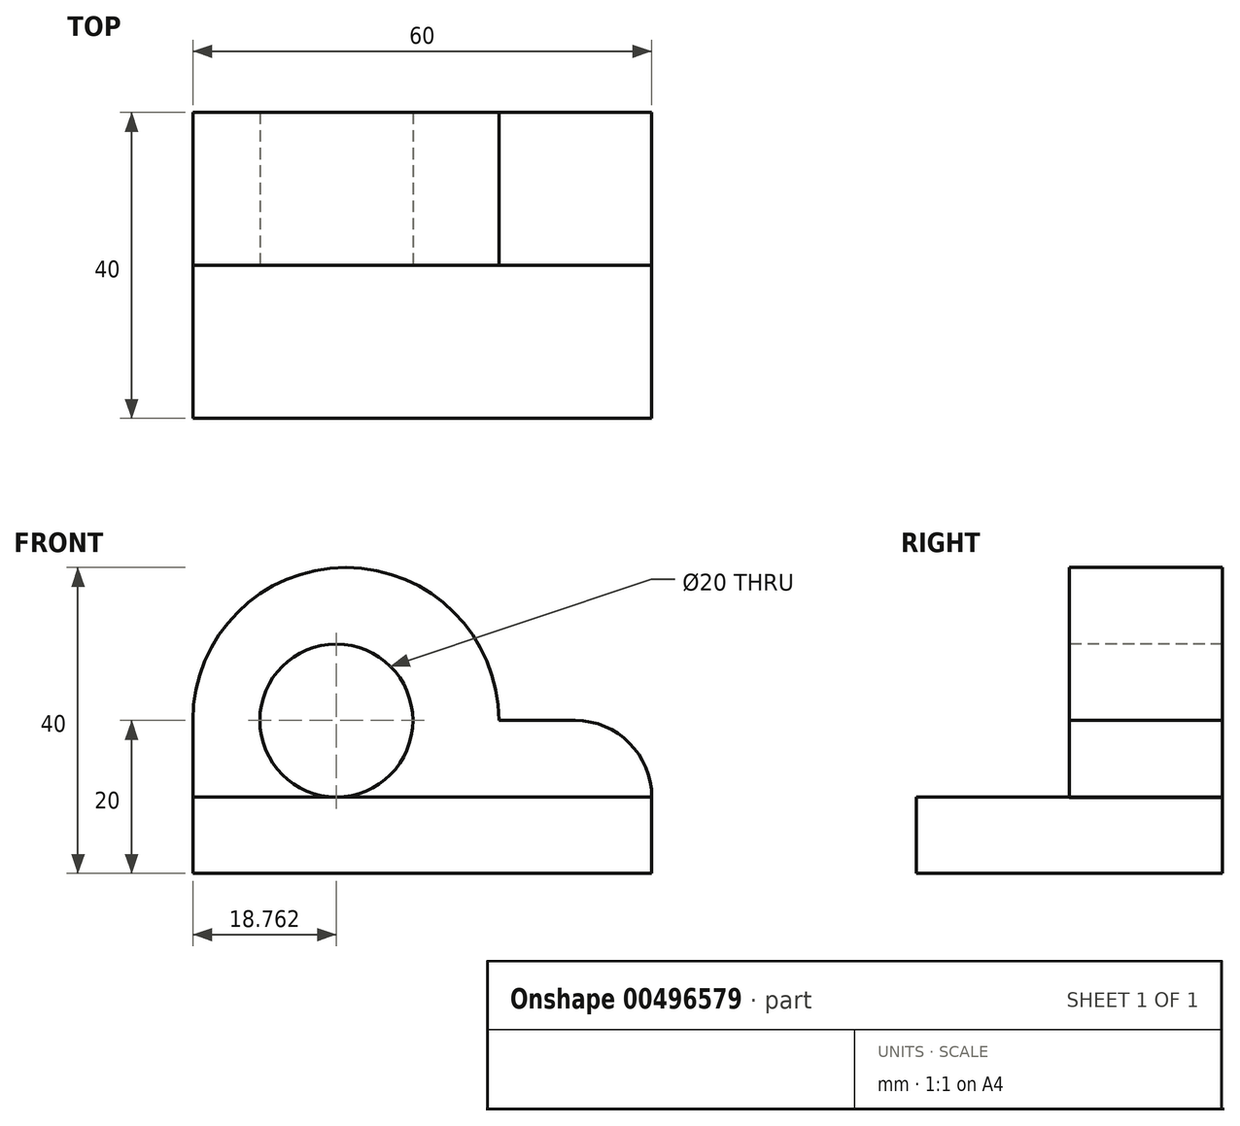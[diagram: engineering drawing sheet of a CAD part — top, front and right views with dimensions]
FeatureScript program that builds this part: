
annotation { "Feature Type Name" : "Feature", "Feature Type Description" : "" }
export const myFeature = defineFeature(function(context is Context, id is Id, definition is map)
    precondition{}
    {
        {
            var Q0;
            Q0=qCreatedBy(makeId("Top.planeOp"),FACE);
            var sketch = newSketch(context, id + "F0", { "sketchPlane" : qUnion([Q0])});
            skLineSegment(sketch, "E0.bottom", {"start": v(0, 0) * mm, "end": v(60, 0) * mm});
            skLineSegment(sketch, "E0.top", {"start": v(0, 40) * mm, "end": v(60, 40) * mm});
            skLineSegment(sketch, "E0.left", {"start": v(0, 0) * mm, "end": v(0, 40) * mm});
            skLineSegment(sketch, "E0.right", {"start": v(60, 0) * mm, "end": v(60, 40) * mm});
            skSolve(sketch);
        }
        {
            var Q0;
            Q0 = qSketchRegion(id + "F0", true);
            extrude(context, id + "F1", {"entities" : qUnion([Q0]), "depth" : 10 * mm});
        }
        {
            var Q0;
            Q0=qCreatedBy(makeId("Front.planeOp"),FACE);
            var sketch = newSketch(context, id + "F2", { "sketchPlane" : qUnion([Q0])});
            skPoint(sketch, "E1", {"position": v(20, 20) * mm});
            skArc(sketch, "E2", {"start": v(40, 20) * mm, "mid": v(20, 40) * mm, "end": v(0, 20) * mm});
            skLineSegment(sketch, "E3", {"start": v(0, 9.95) * mm, "end": v(0, 20) * mm});
            skLineSegment(sketch, "E4", {"start": v(40, 20) * mm, "end": v(50, 20) * mm});
            skLineSegment(sketch, "E5", {"start": v(60, 10) * mm, "end": v(60, 9.95) * mm});
            skLineSegment(sketch, "E6", {"start": v(60, 9.95) * mm, "end": v(0, 9.95) * mm});
            skPoint(sketch, "E7.visualSharp", {"position": v(60, 20) * mm});
            skArc(sketch, "E7.filletArc", {"start": v(60, 10) * mm, "mid": v(57.07, 17.07) * mm, "end": v(50, 20) * mm});
            skSolve(sketch);
        }
        {
            var Q0;
            Q0 = qSketchRegion(id + "F2", true);
            extrude(context, id + "F3", {"entities" : qUnion([Q0]), "oppositeDirection" : true, "depth" : 40 * mm, "hasSecondDirection" : true, "secondDirectionOppositeDirection" : true, "secondDirectionDepth" : 20 * mm});
        }
        {
            var Q0;
            Q0=makeQuery(id+"F3.opExtrude","CAP_FACE",FACE,{"disambiguationData":[OSD([sQuery(id+"F2.wireOp",EDGE,"E2"),sQuery(id+"F2.wireOp",EDGE,"E3"),sQuery(id+"F2.wireOp",EDGE,"E4"),sQuery(id+"F2.wireOp",EDGE,"E6"),sQuery(id+"F2.wireOp",EDGE,"E7.filletArc")])],"isStart":true});
            var sketch = newSketch(context, id + "F4", { "sketchPlane" : qUnion([Q0])});
            skCircle(sketch, "E8", {"center": v(18.76, 20) * mm, "radius": 10 * mm});
            skSolve(sketch);
        }
        {
            var Q0;
            Q0 = qSketchRegion(id + "F4", true);
            extrude(context, id + "F5", {"entities" : qUnion([Q0]), "operationType" : NewBodyOperationType.REMOVE, "oppositeDirection" : true, "depth" : 25 * mm});
        }
    });
